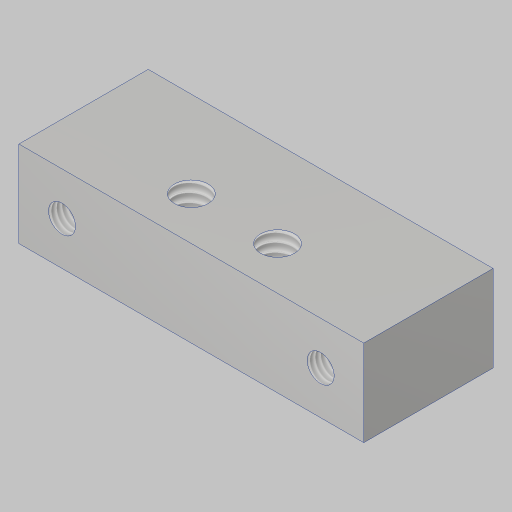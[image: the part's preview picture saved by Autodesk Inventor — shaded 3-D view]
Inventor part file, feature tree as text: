
AUTODESK INVENTOR PART (.ipt)
format: ipt  version: 2023.5 (Build 275446000, 446)  size: 138,240 bytes
history: native  units: in
note: dims shown in document units (in); Inventor stores cm internally (conversion verified against a paired STEP export)
features: sketch x3, hole x2, extrude x1
ambient origin geometry x8: Origin, YZ Plane, XZ Plane, XY Plane, X Axis, Y Axis, Z Axis, Center Point
bodies: Solid1 (feature_tree)
feature tree (6):
  extrude  "Extrusion1"  Depth=0.5in
  hole  "Hole1"  [1 undecoded]
  hole  "Hole2"  [1 undecoded]
  sketch  "Sketch1"  dims[d0=2.0in d1=0.5in]
  sketch  "Sketch2"  dims[d2=0.75in d3=0.0in d4=0.5in]
  sketch  "Sketch3"  dims[d5=0.196in d6=0.5in d7=0.385in d8=0.25in d9=0.5635in d10=1.0in d11=0.8108in d12=1.5in d13=0.156in d14=0.38in d15=0.375in d16=0.25in d17=0.5635in d18=1.0in d19=0.8108in d20=0.25in]
note: 2 required parameter values undecoded (feature->parameter linkage not recoverable at this tier; creation-order binding heuristic only, values carry confidence <= 0.55)
